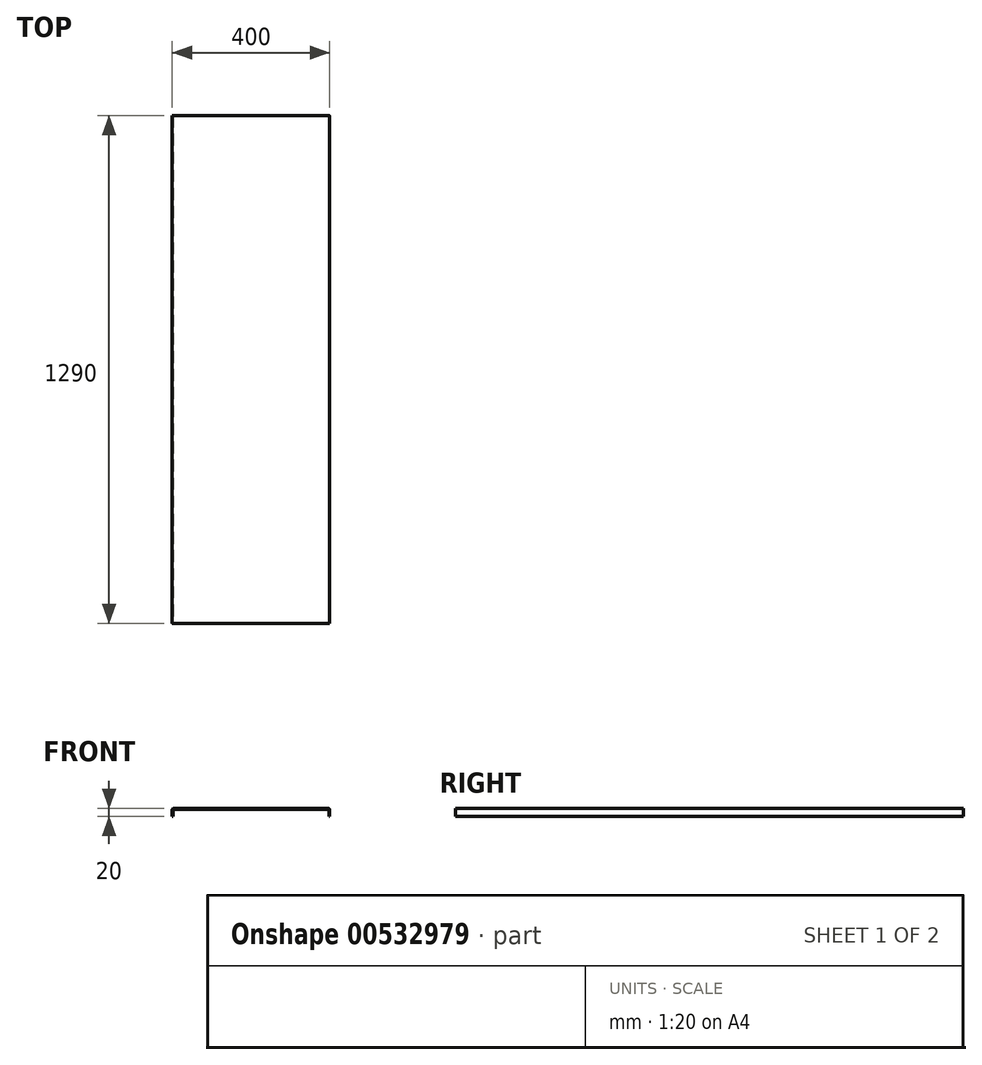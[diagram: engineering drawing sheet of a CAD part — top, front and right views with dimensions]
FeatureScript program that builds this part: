
annotation { "Feature Type Name" : "Feature", "Feature Type Description" : "" }
export const myFeature = defineFeature(function(context is Context, id is Id, definition is map)
    precondition{}
    {
        {
            var Q0;
            Q0=qCreatedBy(makeId("Front.planeOp"),FACE);
            var sketch = newSketch(context, id + "F0", { "sketchPlane" : qUnion([Q0])});
            skLineSegment(sketch, "E0", {"start": v(-107.9, 0) * mm, "end": v(-107.9, 16) * mm});
            skLineSegment(sketch, "E1", {"start": v(-103.9, 20) * mm, "end": v(288.1, 20) * mm});
            skLineSegment(sketch, "E2", {"start": v(292.1, 16) * mm, "end": v(292.1, 0) * mm});
            skLineSegment(sketch, "E3.0", {"start": v(-105.9, 0) * mm, "end": v(-105.9, 16) * mm});
            skLineSegment(sketch, "E4.0", {"start": v(-103.9, 18) * mm, "end": v(288.1, 18) * mm});
            skLineSegment(sketch, "E5.0", {"start": v(290.1, 16) * mm, "end": v(290.1, 0) * mm});
            skLineSegment(sketch, "E6", {"start": v(290.1, 0) * mm, "end": v(292.1, 0) * mm});
            skLineSegment(sketch, "E7", {"start": v(-107.9, 0) * mm, "end": v(-105.9, 0) * mm});
            skPoint(sketch, "E8.visualSharp", {"position": v(-105.9, 18) * mm});
            skArc(sketch, "E8.filletArc", {"start": v(-103.9, 18) * mm, "mid": v(-105.32, 17.41) * mm, "end": v(-105.9, 16) * mm});
            skPoint(sketch, "E9.visualSharp", {"position": v(290.1, 18) * mm});
            skArc(sketch, "E9.filletArc", {"start": v(290.1, 16) * mm, "mid": v(289.5, 17.41) * mm, "end": v(288.1, 18) * mm});
            skPoint(sketch, "E10.visualSharp", {"position": v(292.1, 20) * mm});
            skArc(sketch, "E10.filletArc", {"start": v(292.1, 16) * mm, "mid": v(290.92, 18.83) * mm, "end": v(288.1, 20) * mm});
            skPoint(sketch, "E11.visualSharp", {"position": v(-107.9, 20) * mm});
            skArc(sketch, "E11.filletArc", {"start": v(-103.9, 20) * mm, "mid": v(-106.74, 18.83) * mm, "end": v(-107.9, 16) * mm});
            skSolve(sketch);
        }
        {
            var Q0;
            Q0=makeQuery(id+"F0.imprint","IMPRINT",FACE,{"disambiguationData":[TD([[makeQuery(id+"F0.imprint","IMPRINT",EDGE,{"derivedFrom":sQuery(id+"F0.wireOp",EDGE,"E0")}),-1.0]])]});
            extrude(context, id + "F1", {"entities" : qUnion([Q0]), "oppositeDirection" : true, "depth" : 1290 * mm, "offsetDistance" : 25 * mm});
        }
    });
